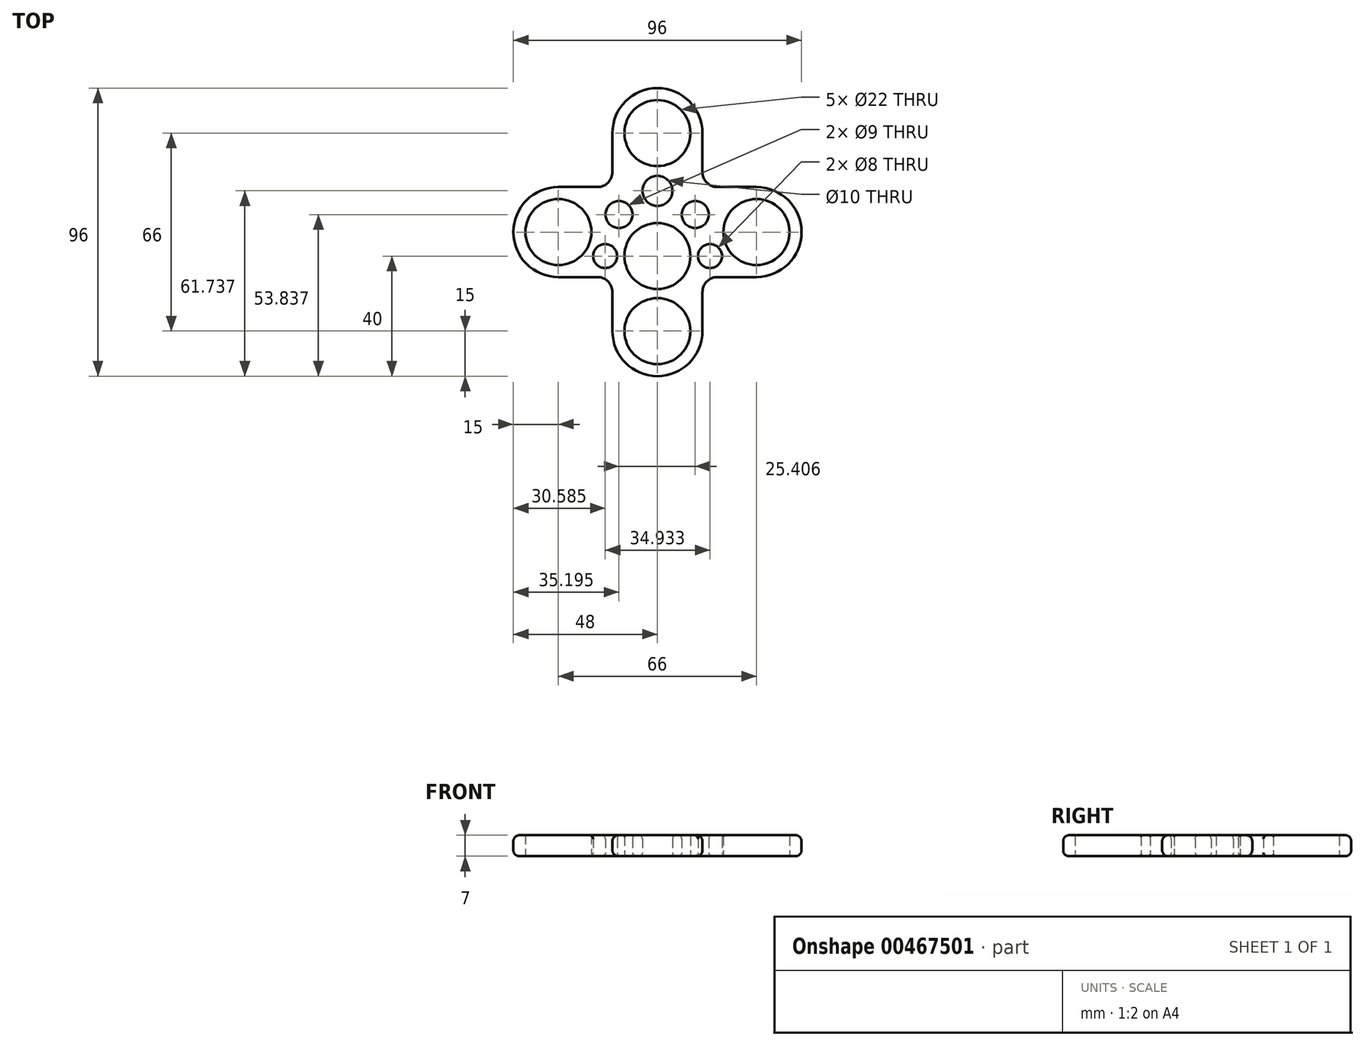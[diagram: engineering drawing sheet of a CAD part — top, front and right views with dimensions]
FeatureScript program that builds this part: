
annotation { "Feature Type Name" : "Feature", "Feature Type Description" : "" }
export const myFeature = defineFeature(function(context is Context, id is Id, definition is map)
    precondition{}
    {
        {
            var Q0;
            Q0=qCreatedBy(makeId("Top.planeOp"),FACE);
            var sketch = newSketch(context, id + "F0", { "sketchPlane" : qUnion([Q0])});
            skCircle(sketch, "E0", {"center": v(0, 41) * mm, "radius": 11 * mm});
            skLineSegment(sketch, "E1", {"start": v(0, 0) * mm, "end": v(0, 41) * mm, "construction": true});
            skCircle(sketch, "E2", {"center": v(0, 41) * mm, "radius": 15 * mm});
            skCircle(sketch, "E3", {"center": v(0, 0) * mm, "radius": 11 * mm});
            skLineSegment(sketch, "E4", {"start": v(-15, 41) * mm, "end": v(-15, 0) * mm});
            skLineSegment(sketch, "E5", {"start": v(15, 41) * mm, "end": v(15, 0) * mm});
            skLineSegment(sketch, "E6", {"start": v(-15, 0) * mm, "end": v(15, 0) * mm});
            skLineSegment(sketch, "E7.1.0", {"start": v(-33, -7) * mm, "end": v(8, -7) * mm});
            skCircle(sketch, "E7.1.1", {"center": v(-33, 8) * mm, "radius": 15 * mm});
            skCircle(sketch, "E7.1.2", {"center": v(-33, 8) * mm, "radius": 11 * mm});
            skLineSegment(sketch, "E7.1.3", {"start": v(-33, 23) * mm, "end": v(8, 23) * mm});
            skPoint(sketch, "E7.1.4", {"position": v(8, 8) * mm});
            skLineSegment(sketch, "E7.2.0", {"start": v(15, -25) * mm, "end": v(15, 16) * mm});
            skCircle(sketch, "E7.2.1", {"center": v(0, -25) * mm, "radius": 15 * mm});
            skCircle(sketch, "E7.2.2", {"center": v(0, -25) * mm, "radius": 11 * mm});
            skLineSegment(sketch, "E7.2.3", {"start": v(-15, -25) * mm, "end": v(-15, 16) * mm});
            skPoint(sketch, "E7.2.4", {"position": v(0, 16) * mm});
            skLineSegment(sketch, "E7.3.0", {"start": v(33, 23) * mm, "end": v(-8, 23) * mm});
            skCircle(sketch, "E7.3.1", {"center": v(33, 8) * mm, "radius": 15 * mm});
            skCircle(sketch, "E7.3.2", {"center": v(33, 8) * mm, "radius": 11 * mm});
            skLineSegment(sketch, "E7.3.3", {"start": v(33, -7) * mm, "end": v(-8, -7) * mm});
            skPoint(sketch, "E7.3.4", {"position": v(-8, 8) * mm});
            skPoint(sketch, "E7.center", {"position": v(0, 8) * mm});
            skCircle(sketch, "E8", {"center": v(12.6, 13.84) * mm, "radius": 4.5 * mm});
            skCircle(sketch, "E9", {"center": v(-12.8, 13.84) * mm, "radius": 4.5 * mm});
            skCircle(sketch, "E10", {"center": v(0, 21.74) * mm, "radius": 5 * mm});
            skCircle(sketch, "E11", {"center": v(-17.42, 0) * mm, "radius": 4 * mm});
            skCircle(sketch, "E12", {"center": v(17.52, 0) * mm, "radius": 4 * mm});
            skLineSegment(sketch, "E13", {"start": v(-12.8, 13.84) * mm, "end": v(15, 13.84) * mm, "construction": true});
            skSolve(sketch);
        }
        {
            var Q0;
            Q0=makeQuery(id+"F0.imprint","IMPRINT",FACE,{"disambiguationData":[TD([[makeQuery(id+"F0.imprint","IMPRINT",EDGE,{"derivedFrom":sQuery(id+"F0.wireOp",EDGE,"36e7d391-d642-43d3-ac27-a5ee1db5424b.1.0")}),-1.0]])]});
            var Q1;
            {var subQ7=sQuery(id+"F0.wireOp",EDGE,"E6");var subQ10=sQuery(id+"F0.wireOp",EDGE,"E3");var subQ14=makeQuery(id+"F0.imprint","INTERSECT",VERTEX,{"disambiguationData":[OD(0.0)],"derivedFrom":[subQ10,subQ7]});Q1=makeQuery(id+"F0.imprint","IMPRINT",FACE,{"disambiguationData":[TD([[makeQuery(id+"F0.imprint","IMPRINT",EDGE,{"disambiguationData":[TD([[subQ14,-1.0]])],"derivedFrom":subQ10}),-1.0]])]});}
            var Q2;
            Q2=makeQuery(id+"F0.imprint","IMPRINT",FACE,{"disambiguationData":[TD([[makeQuery(id+"F0.imprint","IMPRINT",EDGE,{"derivedFrom":sQuery(id+"F0.wireOp",EDGE,"36e7d391-d642-43d3-ac27-a5ee1db5424b.2.0")}),-1.0]])]});
            var Q3;
            {var subQ1=sQuery(id+"F0.wireOp",EDGE,"E4");var subQ4=sQuery(id+"F0.wireOp",EDGE,"E2");var subQ5=makeQuery(id+"F0.imprint","INTERSECT",VERTEX,{"derivedFrom":[subQ4,subQ1]});Q3=makeQuery(id+"F0.imprint","IMPRINT",FACE,{"disambiguationData":[TD([[makeQuery(id+"F0.imprint","IMPRINT",EDGE,{"disambiguationData":[TD([[subQ5,-1.0]])],"derivedFrom":subQ4}),-1.0]])]});}
            var Q4;
            Q4=makeQuery(id+"F0.imprint","IMPRINT",FACE,{"disambiguationData":[TD([[makeQuery(id+"F0.imprint","IMPRINT",EDGE,{"derivedFrom":sQuery(id+"F0.wireOp",EDGE,"E0")}),-1.0]])]});
            var Q5;
            Q5=makeQuery(id+"F0.imprint","IMPRINT",FACE,{"disambiguationData":[TD([[makeQuery(id+"F0.imprint","IMPRINT",EDGE,{"derivedFrom":sQuery(id+"F0.wireOp",EDGE,"E7.1.2")}),-1.0]])]});
            var Q6;
            {var subQ0=sQuery(id+"F0.wireOp",EDGE,"E7.1.3");var subQ1=sQuery(id+"F0.wireOp",EDGE,"E2");var subQ2=makeQuery(id+"F0.imprint","INTERSECT",VERTEX,{"derivedFrom":[subQ1,subQ0]});Q6=makeQuery(id+"F0.imprint","IMPRINT",FACE,{"disambiguationData":[TD([[makeQuery(id+"F0.imprint","IMPRINT",EDGE,{"disambiguationData":[TD([[subQ2,-1.0]])],"derivedFrom":subQ1}),1.0]])]});}
            var Q7;
            {var subQ1=sQuery(id+"F0.wireOp",EDGE,"E4");var subQ3=sQuery(id+"F0.wireOp",EDGE,"E7.1.1");var subQ4=makeQuery(id+"F0.imprint","INTERSECT",VERTEX,{"derivedFrom":[subQ1,subQ3]});Q7=makeQuery(id+"F0.imprint","IMPRINT",FACE,{"disambiguationData":[TD([[makeQuery(id+"F0.imprint","IMPRINT",EDGE,{"disambiguationData":[TD([[subQ4,1.0]])],"derivedFrom":subQ3}),1.0]])]});}
            var Q8;
            {var subQ1=sQuery(id+"F0.wireOp",EDGE,"E6");var subQ3=sQuery(id+"F0.wireOp",EDGE,"E7.1.1");var subQ4=makeQuery(id+"F0.imprint","INTERSECT",VERTEX,{"derivedFrom":[subQ1,subQ3]});Q8=makeQuery(id+"F0.imprint","IMPRINT",FACE,{"disambiguationData":[TD([[makeQuery(id+"F0.imprint","IMPRINT",EDGE,{"disambiguationData":[TD([[subQ4,1.0]])],"derivedFrom":subQ3}),1.0]])]});}
            var Q9;
            Q9=makeQuery(id+"F0.imprint","IMPRINT",FACE,{"disambiguationData":[TD([[makeQuery(id+"F0.imprint","IMPRINT",EDGE,{"derivedFrom":sQuery(id+"F0.wireOp",EDGE,"E7.3.2")}),-1.0]])]});
            var Q10;
            {var subQ0=sQuery(id+"F0.wireOp",EDGE,"E7.3.3");var subQ1=sQuery(id+"F0.wireOp",EDGE,"E7.2.0");var subQ2=makeQuery(id+"F0.imprint","INTERSECT",VERTEX,{"derivedFrom":[subQ1,subQ0]});Q10=makeQuery(id+"F0.imprint","IMPRINT",FACE,{"disambiguationData":[TD([[makeQuery(id+"F0.imprint","IMPRINT",EDGE,{"disambiguationData":[TD([[subQ2,-1.0]])],"derivedFrom":subQ1}),-1.0]])]});}
            var Q11;
            {var subQ1=sQuery(id+"F0.wireOp",EDGE,"E6");var subQ3=sQuery(id+"F0.wireOp",EDGE,"E7.3.1");var subQ4=makeQuery(id+"F0.imprint","INTERSECT",VERTEX,{"derivedFrom":[subQ1,subQ3]});Q11=makeQuery(id+"F0.imprint","IMPRINT",FACE,{"disambiguationData":[TD([[makeQuery(id+"F0.imprint","IMPRINT",EDGE,{"disambiguationData":[TD([[subQ4,-1.0]])],"derivedFrom":subQ3}),1.0]])]});}
            var Q12;
            {var subQ1=sQuery(id+"F0.wireOp",EDGE,"E5");var subQ3=sQuery(id+"F0.wireOp",EDGE,"E7.3.1");var subQ4=makeQuery(id+"F0.imprint","INTERSECT",VERTEX,{"derivedFrom":[subQ1,subQ3]});Q12=makeQuery(id+"F0.imprint","IMPRINT",FACE,{"disambiguationData":[TD([[makeQuery(id+"F0.imprint","IMPRINT",EDGE,{"disambiguationData":[TD([[subQ4,-1.0]])],"derivedFrom":subQ3}),1.0]])]});}
            var Q13;
            {var subQ0=sQuery(id+"F0.wireOp",EDGE,"E7.3.0");var subQ1=sQuery(id+"F0.wireOp",EDGE,"E5");var subQ2=makeQuery(id+"F0.imprint","INTERSECT",VERTEX,{"derivedFrom":[subQ1,subQ0]});Q13=makeQuery(id+"F0.imprint","IMPRINT",FACE,{"disambiguationData":[TD([[makeQuery(id+"F0.imprint","IMPRINT",EDGE,{"disambiguationData":[TD([[subQ2,-1.0]])],"derivedFrom":subQ1}),1.0]])]});}
            var Q14;
            {var subQ0=sQuery(id+"F0.wireOp",EDGE,"E5");var subQ1=sQuery(id+"F0.wireOp",EDGE,"E2");var subQ2=makeQuery(id+"F0.imprint","INTERSECT",VERTEX,{"derivedFrom":[subQ1,subQ0]});Q14=makeQuery(id+"F0.imprint","IMPRINT",FACE,{"disambiguationData":[TD([[makeQuery(id+"F0.imprint","IMPRINT",EDGE,{"disambiguationData":[TD([[subQ2,1.0]])],"derivedFrom":subQ1}),-1.0]])]});}
            var Q15;
            Q15=makeQuery(id+"F0.imprint","IMPRINT",FACE,{"disambiguationData":[TD([[makeQuery(id+"F0.imprint","IMPRINT",EDGE,{"derivedFrom":sQuery(id+"F0.wireOp",EDGE,"E7.2.2")}),-1.0]])]});
            var Q16;
            {var subQ0=sQuery(id+"F0.wireOp",EDGE,"E7.2.1");var subQ1=sQuery(id+"F0.wireOp",EDGE,"E7.2.0");var subQ2=makeQuery(id+"F0.imprint","INTERSECT",VERTEX,{"derivedFrom":[subQ1,subQ0]});Q16=makeQuery(id+"F0.imprint","IMPRINT",FACE,{"disambiguationData":[TD([[makeQuery(id+"F0.imprint","IMPRINT",EDGE,{"disambiguationData":[TD([[subQ2,-1.0]])],"derivedFrom":subQ1}),1.0]])]});}
            var Q17;
            {var subQ0=sQuery(id+"F0.wireOp",EDGE,"E7.2.3");var subQ1=sQuery(id+"F0.wireOp",EDGE,"E7.1.0");var subQ2=makeQuery(id+"F0.imprint","INTERSECT",VERTEX,{"derivedFrom":[subQ1,subQ0]});Q17=makeQuery(id+"F0.imprint","IMPRINT",FACE,{"disambiguationData":[TD([[makeQuery(id+"F0.imprint","IMPRINT",EDGE,{"disambiguationData":[TD([[subQ2,-1.0]])],"derivedFrom":subQ1}),-1.0]])]});}
            var Q18;
            {var subQ0=sQuery(id+"F0.wireOp",EDGE,"E7.1.1");var subQ1=sQuery(id+"F0.wireOp",EDGE,"E7.1.0");var subQ2=makeQuery(id+"F0.imprint","INTERSECT",VERTEX,{"derivedFrom":[subQ1,subQ0]});Q18=makeQuery(id+"F0.imprint","IMPRINT",FACE,{"disambiguationData":[TD([[makeQuery(id+"F0.imprint","IMPRINT",EDGE,{"disambiguationData":[TD([[subQ2,-1.0]])],"derivedFrom":subQ1}),1.0]])]});}
            var Q19;
            {var subQ0=sQuery(id+"F0.wireOp",EDGE,"E7.1.3");var subQ1=sQuery(id+"F0.wireOp",EDGE,"E4");var subQ2=makeQuery(id+"F0.imprint","INTERSECT",VERTEX,{"derivedFrom":[subQ1,subQ0]});Q19=makeQuery(id+"F0.imprint","IMPRINT",FACE,{"disambiguationData":[TD([[makeQuery(id+"F0.imprint","IMPRINT",EDGE,{"disambiguationData":[TD([[subQ2,-1.0]])],"derivedFrom":subQ1}),-1.0]])]});}
            var Q20;
            {var subQ8=sQuery(id+"F0.wireOp",EDGE,"E7.3.0");var subQ12=makeQuery(id+"F0.imprint","IMPRINT",VERTEX,{"derivedFrom":subQ8});Q20=makeQuery(id+"F0.imprint","IMPRINT",FACE,{"disambiguationData":[TD([[makeQuery(id+"F0.imprint","IMPRINT",EDGE,{"disambiguationData":[TD([[subQ12,1.0]])],"derivedFrom":subQ8}),1.0]])]});}
            var Q21;
            {var subQ0=sQuery(id+"F0.wireOp",EDGE,"E6");var subQ1=sQuery(id+"F0.wireOp",EDGE,"E3");var subQ2=makeQuery(id+"F0.imprint","INTERSECT",VERTEX,{"disambiguationData":[OD(1.0)],"derivedFrom":[subQ1,subQ0]});Q21=makeQuery(id+"F0.imprint","IMPRINT",FACE,{"disambiguationData":[TD([[makeQuery(id+"F0.imprint","IMPRINT",EDGE,{"disambiguationData":[TD([[subQ2,1.0]])],"derivedFrom":subQ1}),-1.0]])]});}
            var Q22;
            {var subQ0=sQuery(id+"F0.wireOp",EDGE,"E7.1.3");var subQ1=sQuery(id+"F0.wireOp",EDGE,"E4");var subQ2=makeQuery(id+"F0.imprint","INTERSECT",VERTEX,{"derivedFrom":[subQ1,subQ0]});Q22=makeQuery(id+"F0.imprint","IMPRINT",FACE,{"disambiguationData":[TD([[makeQuery(id+"F0.imprint","IMPRINT",EDGE,{"disambiguationData":[TD([[subQ2,-1.0]])],"derivedFrom":subQ1}),1.0]])]});}
            extrude(context, id + "F1", {"entities" : qUnion([Q0, Q1, Q2, Q3, Q4, Q5, Q6, Q7, Q8, Q9, Q10, Q11, Q12, Q13, Q14, Q15, Q16, Q17, Q18, Q19, Q20, Q21, Q22]), "depth" : 7 * mm, "offsetDistance" : 25 * mm});
        }
        {
            var Q0;
            Q0=makeQuery(id+"F1.opExtrude","SWEPT_EDGE",EDGE,{"disambiguationData":[OSD([sQuery(id+"F0.wireOp",EDGE,"E4"),sQuery(id+"F0.wireOp",EDGE,"36e7d391-d642-43d3-ac27-a5ee1db5424b.1.2")])]});
            var Q1;
            Q1=makeQuery(id+"F1.opExtrude","SWEPT_EDGE",EDGE,{"disambiguationData":[OSD([sQuery(id+"F0.wireOp",EDGE,"E5"),sQuery(id+"F0.wireOp",EDGE,"36e7d391-d642-43d3-ac27-a5ee1db5424b.2.3")])]});
            var Q2;
            Q2=makeQuery(id+"F1.opExtrude","SWEPT_EDGE",EDGE,{"disambiguationData":[OSD([sQuery(id+"F0.wireOp",EDGE,"36e7d391-d642-43d3-ac27-a5ee1db5424b.1.3"),sQuery(id+"F0.wireOp",EDGE,"36e7d391-d642-43d3-ac27-a5ee1db5424b.2.2")])]});
            var Q3;
            Q3=makeQuery(id+"F1.opExtrude","SWEPT_EDGE",EDGE,{"disambiguationData":[OSD([sQuery(id+"F0.wireOp",EDGE,"E7.2.0"),sQuery(id+"F0.wireOp",EDGE,"E7.3.3")])]});
            var Q4;
            Q4=makeQuery(id+"F1.opExtrude","SWEPT_EDGE",EDGE,{"disambiguationData":[OSD([sQuery(id+"F0.wireOp",EDGE,"E7.1.0"),sQuery(id+"F0.wireOp",EDGE,"E7.2.3")])]});
            fillet(context, id + "F2", {"entities" : qUnion([Q0, Q1, Q2, Q3, Q4]), "radius" : 5 * mm, "tangentPropagation" : true, "allowEdgeOverflow" : false});
        }
        {
            var Q0;
            Q0=makeQuery(id+"F1.opExtrude","CAP_EDGE",EDGE,{"disambiguationData":[OSD([sQuery(id+"F0.wireOp",EDGE,"E0")])],"isStart":false});
            var Q1;
            Q1=makeQuery(id+"F1.opExtrude","CAP_EDGE",EDGE,{"disambiguationData":[OSD([sQuery(id+"F0.wireOp",EDGE,"E3")])],"isStart":false});
            var Q2;
            Q2=makeQuery(id+"F1.opExtrude","CAP_EDGE",EDGE,{"disambiguationData":[OSD([sQuery(id+"F0.wireOp",EDGE,"36e7d391-d642-43d3-ac27-a5ee1db5424b.1.0")])],"isStart":false});
            var Q3;
            Q3=makeQuery(id+"F1.opExtrude","CAP_EDGE",EDGE,{"disambiguationData":[OSD([sQuery(id+"F0.wireOp",EDGE,"36e7d391-d642-43d3-ac27-a5ee1db5424b.2.0")])],"isStart":false});
            var Q4;
            Q4=makeQuery(id+"F1.opExtrude","CAP_EDGE",EDGE,{"disambiguationData":[OSD([sQuery(id+"F0.wireOp",EDGE,"36e7d391-d642-43d3-ac27-a5ee1db5424b.1.0")])],"isStart":true});
            var Q5;
            Q5=makeQuery(id+"F1.opExtrude","CAP_EDGE",EDGE,{"disambiguationData":[OSD([sQuery(id+"F0.wireOp",EDGE,"E0")])],"isStart":true});
            var Q6;
            Q6=makeQuery(id+"F1.opExtrude","CAP_EDGE",EDGE,{"disambiguationData":[OSD([sQuery(id+"F0.wireOp",EDGE,"36e7d391-d642-43d3-ac27-a5ee1db5424b.2.0")])],"isStart":true});
            var Q7;
            Q7=makeQuery(id+"F1.opExtrude","CAP_EDGE",EDGE,{"disambiguationData":[OSD([sQuery(id+"F0.wireOp",EDGE,"E3")])],"isStart":true});
            var Q8;
            Q8=makeQuery(id+"F1.opExtrude","CAP_EDGE",EDGE,{"disambiguationData":[OSD([sQuery(id+"F0.wireOp",EDGE,"E7.2.2")])],"isStart":false});
            var Q9;
            Q9=makeQuery(id+"F1.opExtrude","CAP_EDGE",EDGE,{"disambiguationData":[OSD([sQuery(id+"F0.wireOp",EDGE,"E7.1.2")])],"isStart":true});
            var Q10;
            Q10=makeQuery(id+"F1.opExtrude","CAP_EDGE",EDGE,{"disambiguationData":[OSD([sQuery(id+"F0.wireOp",EDGE,"E7.3.2")])],"isStart":true});
            var Q11;
            Q11=makeQuery(id+"F1.opExtrude","CAP_EDGE",EDGE,{"disambiguationData":[OSD([sQuery(id+"F0.wireOp",EDGE,"E7.2.2")])],"isStart":true});
            var Q12;
            Q12=makeQuery(id+"F1.opExtrude","CAP_EDGE",EDGE,{"disambiguationData":[OSD([sQuery(id+"F0.wireOp",EDGE,"E7.3.2")])],"isStart":false});
            fillet(context, id + "F3", {"entities" : qUnion([Q0, Q1, Q2, Q3, Q4, Q5, Q6, Q7, Q8, Q9, Q10, Q11, Q12]), "radius" : .5 * mm, "tangentPropagation" : true, "allowEdgeOverflow" : false});
        }
        {
            var Q0;
            Q0=makeQuery(id+"F1.opExtrude","SWEPT_FACE",FACE,{"disambiguationData":[OSD([sQuery(id+"F0.wireOp",EDGE,"36e7d391-d642-43d3-ac27-a5ee1db5424b.1.3")])]});
            var Q1;
            Q1=makeQuery(id+"F2.opFillet","BLEND_FACE",FACE,{"disambiguationData":[OSD([sQuery(id+"F0.wireOp",EDGE,"36e7d391-d642-43d3-ac27-a5ee1db5424b.1.3"),sQuery(id+"F0.wireOp",EDGE,"36e7d391-d642-43d3-ac27-a5ee1db5424b.2.2")])]});
            var Q2;
            Q2=makeQuery(id+"F1.opExtrude","SWEPT_FACE",FACE,{"disambiguationData":[OSD([sQuery(id+"F0.wireOp",EDGE,"36e7d391-d642-43d3-ac27-a5ee1db5424b.2.2")])]});
            var Q3;
            Q3=makeQuery(id+"F1.opExtrude","SWEPT_FACE",FACE,{"disambiguationData":[OSD([sQuery(id+"F0.wireOp",EDGE,"36e7d391-d642-43d3-ac27-a5ee1db5424b.2.1")])]});
            var Q4;
            Q4=makeQuery(id+"F1.opExtrude","SWEPT_FACE",FACE,{"disambiguationData":[OSD([sQuery(id+"F0.wireOp",EDGE,"36e7d391-d642-43d3-ac27-a5ee1db5424b.1.1")])]});
            var Q5;
            Q5=makeQuery(id+"F1.opExtrude","SWEPT_FACE",FACE,{"disambiguationData":[OSD([sQuery(id+"F0.wireOp",EDGE,"36e7d391-d642-43d3-ac27-a5ee1db5424b.1.2")])]});
            var Q6;
            Q6=makeQuery(id+"F2.opFillet","BLEND_FACE",FACE,{"disambiguationData":[OSD([sQuery(id+"F0.wireOp",EDGE,"E4"),sQuery(id+"F0.wireOp",EDGE,"36e7d391-d642-43d3-ac27-a5ee1db5424b.1.2")])]});
            var Q7;
            Q7=makeQuery(id+"F1.opExtrude","SWEPT_FACE",FACE,{"disambiguationData":[OSD([sQuery(id+"F0.wireOp",EDGE,"E4")])]});
            var Q8;
            Q8=makeQuery(id+"F1.opExtrude","SWEPT_FACE",FACE,{"disambiguationData":[OSD([sQuery(id+"F0.wireOp",EDGE,"E2")])]});
            var Q9;
            Q9=makeQuery(id+"F1.opExtrude","SWEPT_FACE",FACE,{"disambiguationData":[OSD([sQuery(id+"F0.wireOp",EDGE,"E5")])]});
            var Q10;
            Q10=makeQuery(id+"F2.opFillet","BLEND_FACE",FACE,{"disambiguationData":[OSD([sQuery(id+"F0.wireOp",EDGE,"E5"),sQuery(id+"F0.wireOp",EDGE,"36e7d391-d642-43d3-ac27-a5ee1db5424b.2.3")])]});
            var Q11;
            Q11=makeQuery(id+"F1.opExtrude","SWEPT_FACE",FACE,{"disambiguationData":[OSD([sQuery(id+"F0.wireOp",EDGE,"36e7d391-d642-43d3-ac27-a5ee1db5424b.2.3")])]});
            var Q12;
            Q12=makeQuery(id+"F1.opExtrude","CAP_EDGE",EDGE,{"disambiguationData":[OSD([sQuery(id+"F0.wireOp",EDGE,"E7.2.1")])],"isStart":false});
            var Q13;
            Q13=makeQuery(id+"F1.opExtrude","CAP_EDGE",EDGE,{"disambiguationData":[OSD([sQuery(id+"F0.wireOp",EDGE,"E7.2.1")])],"isStart":true});
            var Q14;
            Q14=makeQuery(id+"F1.opExtrude","CAP_EDGE",EDGE,{"disambiguationData":[OSD([sQuery(id+"F0.wireOp",EDGE,"tZJT3DoQ-D1af-9ejb-kBn4-vq431sMQ58al")])],"isStart":false});
            var Q15;
            Q15=makeQuery(id+"F1.opExtrude","CAP_EDGE",EDGE,{"disambiguationData":[OSD([sQuery(id+"F0.wireOp",EDGE,"8KycXkff-1oB4-IYEB-PP2n-TUBcDwQmhNfT")])],"isStart":false});
            var Q16;
            Q16=makeQuery(id+"F1.opExtrude","CAP_EDGE",EDGE,{"disambiguationData":[OSD([sQuery(id+"F0.wireOp",EDGE,"XyrBx8S9-UvYg-jl4D-A59R-dC0e4iYWKspB")])],"isStart":false});
            var Q17;
            Q17=makeQuery(id+"F1.opExtrude","CAP_EDGE",EDGE,{"disambiguationData":[OSD([sQuery(id+"F0.wireOp",EDGE,"rOm6KhEB-D2Yf-xZaN-V1DL-hImf4mlvyvvV")])],"isStart":false});
            var Q18;
            Q18=makeQuery(id+"F1.opExtrude","CAP_EDGE",EDGE,{"disambiguationData":[OSD([sQuery(id+"F0.wireOp",EDGE,"zP1W1kTJ-qeuI-szWn-KxqT-DPLY6Nq33lTA")])],"isStart":false});
            var Q19;
            Q19=makeQuery(id+"F1.opExtrude","CAP_EDGE",EDGE,{"disambiguationData":[OSD([sQuery(id+"F0.wireOp",EDGE,"ZUi09zwu-Gl61-4nxd-UdVw-LttNZ5gOr2Fc")])],"isStart":false});
            var Q20;
            Q20=makeQuery(id+"F1.opExtrude","CAP_EDGE",EDGE,{"disambiguationData":[OSD([sQuery(id+"F0.wireOp",EDGE,"mNmrvGZg-prUN-5nK1-pCQN-ky9igySLdU9A")])],"isStart":false});
            var Q21;
            Q21=makeQuery(id+"F1.opExtrude","CAP_EDGE",EDGE,{"disambiguationData":[OSD([sQuery(id+"F0.wireOp",EDGE,"zKzxMDpB-VPIE-l8cI-pqsk-HU1voQPF6ZFo")])],"isStart":false});
            var Q22;
            Q22=makeQuery(id+"F1.opExtrude","CAP_EDGE",EDGE,{"disambiguationData":[OSD([sQuery(id+"F0.wireOp",EDGE,"aUEOQ63F-tW68-74PS-bJHd-fQbIgY51WiE7")])],"isStart":false});
            var Q23;
            Q23=makeQuery(id+"F1.opExtrude","CAP_EDGE",EDGE,{"disambiguationData":[OSD([sQuery(id+"F0.wireOp",EDGE,"x04RhjGW-dVQO-Px21-tspN-isRoQJ9udYmB")])],"isStart":false});
            var Q24;
            Q24=makeQuery(id+"F1.opExtrude","CAP_EDGE",EDGE,{"disambiguationData":[OSD([sQuery(id+"F0.wireOp",EDGE,"aUEOQ63F-tW68-74PS-bJHd-fQbIgY51WiE7")])],"isStart":true});
            var Q25;
            Q25=makeQuery(id+"F1.opExtrude","CAP_EDGE",EDGE,{"disambiguationData":[OSD([sQuery(id+"F0.wireOp",EDGE,"zKzxMDpB-VPIE-l8cI-pqsk-HU1voQPF6ZFo")])],"isStart":true});
            var Q26;
            Q26=makeQuery(id+"F1.opExtrude","CAP_EDGE",EDGE,{"disambiguationData":[OSD([sQuery(id+"F0.wireOp",EDGE,"mNmrvGZg-prUN-5nK1-pCQN-ky9igySLdU9A")])],"isStart":true});
            var Q27;
            Q27=makeQuery(id+"F1.opExtrude","CAP_EDGE",EDGE,{"disambiguationData":[OSD([sQuery(id+"F0.wireOp",EDGE,"8KycXkff-1oB4-IYEB-PP2n-TUBcDwQmhNfT")])],"isStart":true});
            var Q28;
            Q28=makeQuery(id+"F1.opExtrude","CAP_EDGE",EDGE,{"disambiguationData":[OSD([sQuery(id+"F0.wireOp",EDGE,"XyrBx8S9-UvYg-jl4D-A59R-dC0e4iYWKspB")])],"isStart":true});
            var Q29;
            Q29=makeQuery(id+"F1.opExtrude","CAP_EDGE",EDGE,{"disambiguationData":[OSD([sQuery(id+"F0.wireOp",EDGE,"tZJT3DoQ-D1af-9ejb-kBn4-vq431sMQ58al")])],"isStart":true});
            var Q30;
            Q30=makeQuery(id+"F1.opExtrude","CAP_EDGE",EDGE,{"disambiguationData":[OSD([sQuery(id+"F0.wireOp",EDGE,"rOm6KhEB-D2Yf-xZaN-V1DL-hImf4mlvyvvV")])],"isStart":true});
            var Q31;
            Q31=makeQuery(id+"F1.opExtrude","CAP_EDGE",EDGE,{"disambiguationData":[OSD([sQuery(id+"F0.wireOp",EDGE,"zP1W1kTJ-qeuI-szWn-KxqT-DPLY6Nq33lTA")])],"isStart":true});
            var Q32;
            Q32=makeQuery(id+"F1.opExtrude","CAP_EDGE",EDGE,{"disambiguationData":[OSD([sQuery(id+"F0.wireOp",EDGE,"ZUi09zwu-Gl61-4nxd-UdVw-LttNZ5gOr2Fc")])],"isStart":true});
            var Q33;
            Q33=makeQuery(id+"F1.opExtrude","CAP_EDGE",EDGE,{"disambiguationData":[OSD([sQuery(id+"F0.wireOp",EDGE,"x04RhjGW-dVQO-Px21-tspN-isRoQJ9udYmB")])],"isStart":true});
            var Q34;
            Q34=makeQuery(id+"F1.opExtrude","CAP_EDGE",EDGE,{"disambiguationData":[OSD([sQuery(id+"F0.wireOp",EDGE,"DS8W5hFZ-9TJv-t2lf-6E1Z-6UBaKxHkVqPz")])],"isStart":false});
            var Q35;
            Q35=makeQuery(id+"F1.opExtrude","CAP_EDGE",EDGE,{"disambiguationData":[OSD([sQuery(id+"F0.wireOp",EDGE,"gOQBDpEe-CA2c-9m3L-cOWV-TKasKFnOMsaN")])],"isStart":false});
            var Q36;
            Q36=makeQuery(id+"F1.opExtrude","CAP_EDGE",EDGE,{"disambiguationData":[OSD([sQuery(id+"F0.wireOp",EDGE,"JotSh60F-TzvT-nZG5-UOGx-PqN8K5EzcsqB")])],"isStart":false});
            var Q37;
            Q37=makeQuery(id+"F1.opExtrude","SWEPT_FACE",FACE,{"disambiguationData":[OSD([sQuery(id+"F0.wireOp",EDGE,"N8sLp6BR-k0QI-7QnY-0FU2-Hdd4o4EEy6C8")])]});
            var Q38;
            Q38=makeQuery(id+"F1.opExtrude","CAP_EDGE",EDGE,{"disambiguationData":[OSD([sQuery(id+"F0.wireOp",EDGE,"gOQBDpEe-CA2c-9m3L-cOWV-TKasKFnOMsaN")])],"isStart":true});
            var Q39;
            Q39=makeQuery(id+"F1.opExtrude","CAP_EDGE",EDGE,{"disambiguationData":[OSD([sQuery(id+"F0.wireOp",EDGE,"DS8W5hFZ-9TJv-t2lf-6E1Z-6UBaKxHkVqPz")])],"isStart":true});
            var Q40;
            Q40=makeQuery(id+"F1.opExtrude","CAP_EDGE",EDGE,{"disambiguationData":[OSD([sQuery(id+"F0.wireOp",EDGE,"JotSh60F-TzvT-nZG5-UOGx-PqN8K5EzcsqB")])],"isStart":true});
            fillet(context, id + "F4", {"entities" : qUnion([Q0, Q1, Q2, Q3, Q4, Q5, Q6, Q7, Q8, Q9, Q10, Q11, Q12, Q13, Q14, Q15, Q16, Q17, Q18, Q19, Q20, Q21, Q22, Q23, Q24, Q25, Q26, Q27, Q28, Q29, Q30, Q31, Q32, Q33, Q34, Q35, Q36, Q37, Q38, Q39, Q40]), "radius" : 2 * mm, "tangentPropagation" : true, "allowEdgeOverflow" : false});
        }
        {
            var Q0;
            Q0=makeQuery(id+"F1.opExtrude","SWEPT_FACE",FACE,{"disambiguationData":[OSD([sQuery(id+"F0.wireOp",EDGE,"E12")])]});
            var Q1;
            Q1=makeQuery(id+"F1.opExtrude","SWEPT_FACE",FACE,{"disambiguationData":[OSD([sQuery(id+"F0.wireOp",EDGE,"E8")])]});
            var Q2;
            Q2=makeQuery(id+"F1.opExtrude","SWEPT_FACE",FACE,{"disambiguationData":[OSD([sQuery(id+"F0.wireOp",EDGE,"E10")])]});
            var Q3;
            Q3=makeQuery(id+"F1.opExtrude","SWEPT_FACE",FACE,{"disambiguationData":[OSD([sQuery(id+"F0.wireOp",EDGE,"E9")])]});
            var Q4;
            Q4=makeQuery(id+"F1.opExtrude","SWEPT_FACE",FACE,{"disambiguationData":[OSD([sQuery(id+"F0.wireOp",EDGE,"E11")])]});
            fillet(context, id + "F5", {"entities" : qUnion([Q0, Q1, Q2, Q3, Q4]), "radius" : 1.25 * mm, "tangentPropagation" : true, "allowEdgeOverflow" : false});
        }
    });
